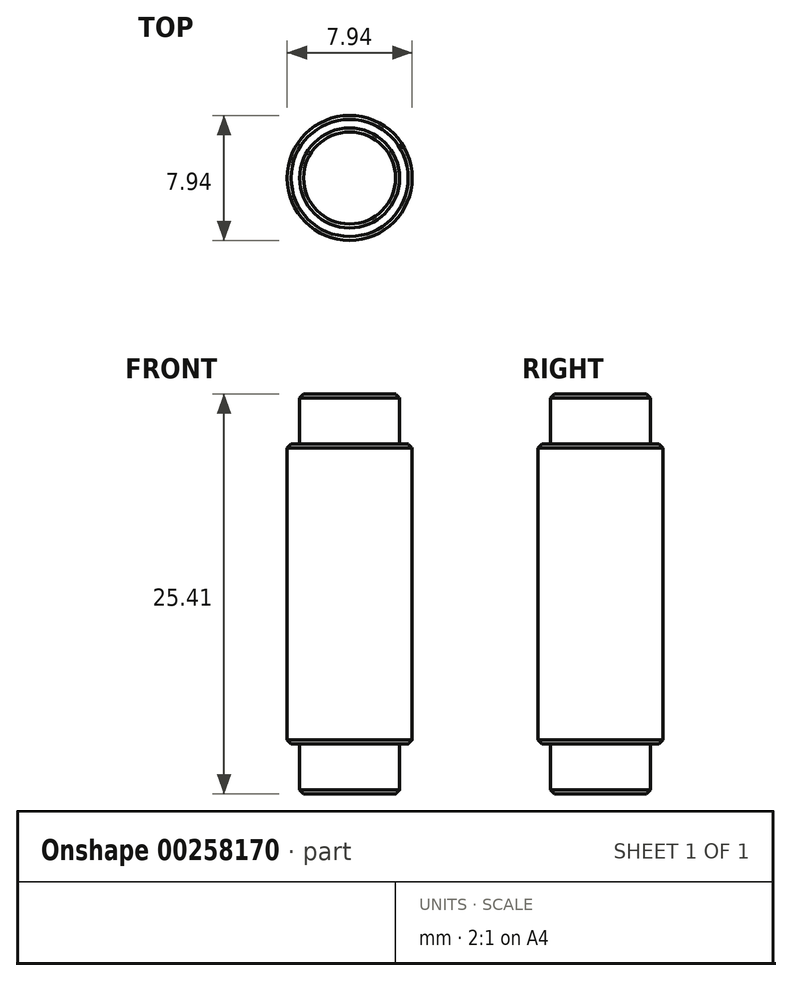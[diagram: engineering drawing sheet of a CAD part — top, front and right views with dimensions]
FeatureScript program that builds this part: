
annotation { "Feature Type Name" : "Feature", "Feature Type Description" : "" }
export const myFeature = defineFeature(function(context is Context, id is Id, definition is map)
    precondition{}
    {
        {
            var Q0;
            Q0=qCreatedBy(makeId("Top.planeOp"),FACE);
            var sketch = newSketch(context, id + "F0", { "sketchPlane" : qUnion([Q0])});
            skCircle(sketch, "E0", {"center": v(0, 0) * mm, "radius": 3.97 * mm});
            skSolve(sketch);
        }
        {
            var Q0;
            Q0 = qSketchRegion(id + "F0", true);
            extrude(context, id + "F1", {"entities" : qUnion([Q0]), "depth" : 19.05 * mm});
        }
        {
            var Q0;
            Q0=qCreatedBy(makeId("Top.planeOp"),FACE);
            var sketch = newSketch(context, id + "F2", { "sketchPlane" : qUnion([Q0])});
            skCircle(sketch, "E1", {"center": v(0, 0) * mm, "radius": 3.18 * mm});
            skSolve(sketch);
        }
        {
            var Q0;
            Q0 = qSketchRegion(id + "F2", true);
            extrude(context, id + "F3", {"entities" : qUnion([Q0]), "operationType" : NewBodyOperationType.ADD, "oppositeDirection" : true, "depth" : 3.17 * mm});
        }
        {
            var Q0;
            Q0=makeQuery(id+"F1.opExtrude","CAP_FACE",FACE,{"disambiguationData":[OSD([sQuery(id+"F0.wireOp",EDGE,"E0")])],"isStart":false});
            var sketch = newSketch(context, id + "F4", { "sketchPlane" : qUnion([Q0])});
            skCircle(sketch, "E2", {"center": v(0, 0) * mm, "radius": 3.18 * mm});
            skSolve(sketch);
        }
        {
            var Q0;
            Q0 = qSketchRegion(id + "F4", true);
            extrude(context, id + "F5", {"entities" : qUnion([Q0]), "operationType" : NewBodyOperationType.ADD, "depth" : 3.17 * mm});
        }
        {
            var Q0;
            Q0=makeQuery(id+"F5.opExtrude","CAP_EDGE",EDGE,{"disambiguationData":[OSD([sQuery(id+"F4.wireOp",EDGE,"E2")])],"isStart":false});
            var Q1;
            Q1=makeQuery(id+"F1.opExtrude","CAP_EDGE",EDGE,{"disambiguationData":[OSD([sQuery(id+"F0.wireOp",EDGE,"E0")])],"isStart":false});
            var Q2;
            Q2=makeQuery(id+"F3.opExtrude","CAP_EDGE",EDGE,{"disambiguationData":[OSD([sQuery(id+"F2.wireOp",EDGE,"E1")])],"isStart":false});
            var Q3;
            Q3=makeQuery(id+"F1.opExtrude","CAP_EDGE",EDGE,{"disambiguationData":[OSD([sQuery(id+"F0.wireOp",EDGE,"E0")])],"isStart":true});
            chamfer(context, id + "F6", {"entities" : qUnion([Q0, Q1, Q2, Q3]), "width" : 0.25 * mm, "tangentPropagation" : true});
        }
    });
